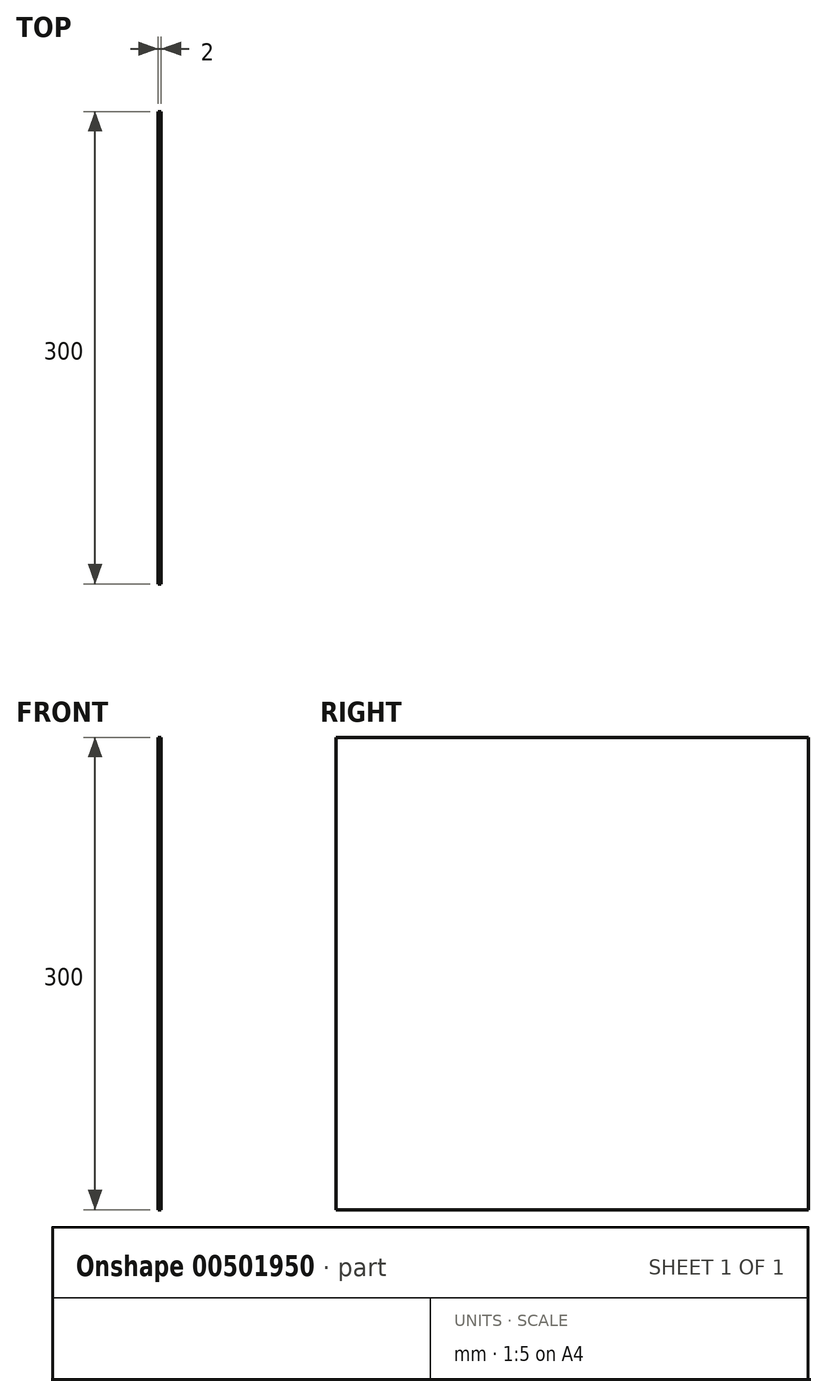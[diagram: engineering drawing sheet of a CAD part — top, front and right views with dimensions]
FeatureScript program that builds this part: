
annotation { "Feature Type Name" : "Feature", "Feature Type Description" : "" }
export const myFeature = defineFeature(function(context is Context, id is Id, definition is map)
    precondition{}
    {
        {
            var Q0;
            Q0=qCreatedBy(makeId("Right.planeOp"),FACE);
            var sketch = newSketch(context, id + "F0", { "sketchPlane" : qUnion([Q0])});
            skLineSegment(sketch, "E0.bottom", {"start": v(150, 150) * mm, "end": v(-150, 150) * mm});
            skLineSegment(sketch, "E0.top", {"start": v(150, -150) * mm, "end": v(-150, -150) * mm});
            skLineSegment(sketch, "E0.left", {"start": v(150, 150) * mm, "end": v(150, -150) * mm});
            skLineSegment(sketch, "E0.right", {"start": v(-150, 150) * mm, "end": v(-150, -150) * mm});
            skPoint(sketch, "E0.middle", {"position": v(0, 0) * mm});
            skSolve(sketch);
        }
        {
            var Q0;
            Q0=makeQuery(id+"F0.imprint","IMPRINT",FACE,{"disambiguationData":[TD([[makeQuery(id+"F0.imprint","IMPRINT",EDGE,{"derivedFrom":sQuery(id+"F0.wireOp",EDGE,"E0.bottom")}),1.0]])]});
            extrude(context, id + "F1", {"entities" : qUnion([Q0]), "depth" : 2 * mm, "symmetric" : true});
        }
    });
